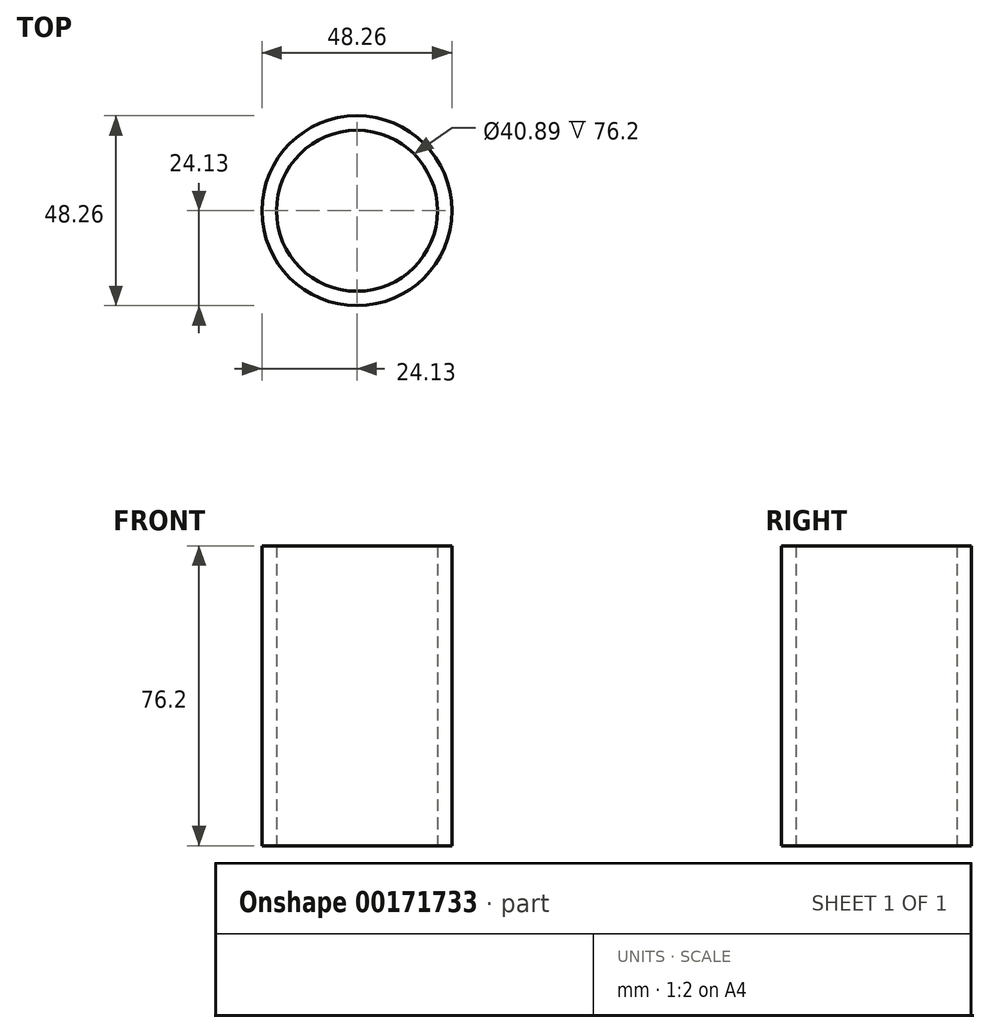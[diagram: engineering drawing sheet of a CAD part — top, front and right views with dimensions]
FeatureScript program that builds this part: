
annotation { "Feature Type Name" : "Feature", "Feature Type Description" : "" }
export const myFeature = defineFeature(function(context is Context, id is Id, definition is map)
    precondition{}
    {
        {
            var Q0;
            Q0=qCreatedBy(makeId("Top.planeOp"),FACE);
            var sketch = newSketch(context, id + "F0", { "sketchPlane" : qUnion([Q0])});
            skCircle(sketch, "E0", {"center": v(0, 0) * mm, "radius": 24.13 * mm});
            skCircle(sketch, "E1", {"center": v(0, 0) * mm, "radius": 20.45 * mm});
            skSolve(sketch);
        }
        {
            var Q0;
            Q0 = qSketchRegion(id + "F0", true);
            extrude(context, id + "F1", {"entities" : qUnion([Q0]), "depth" : 76.2 * mm});
        }
    });
